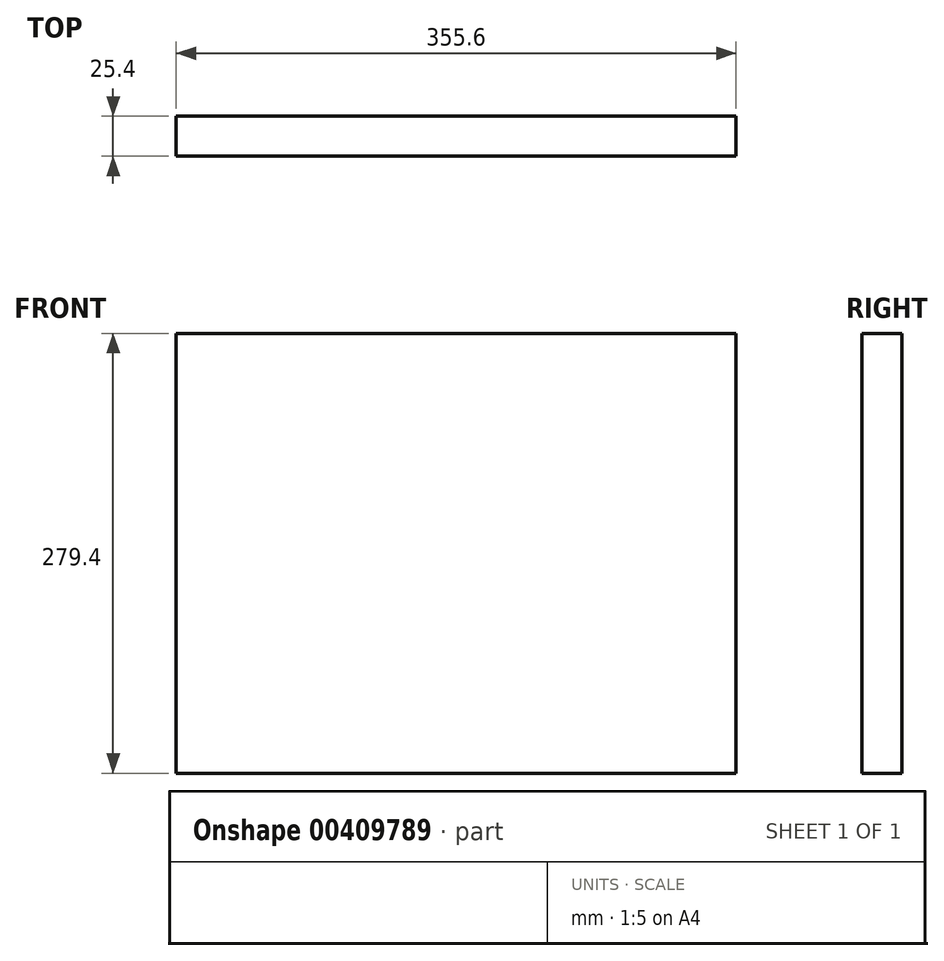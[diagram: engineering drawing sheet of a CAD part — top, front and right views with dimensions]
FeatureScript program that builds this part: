
annotation { "Feature Type Name" : "Feature", "Feature Type Description" : "" }
export const myFeature = defineFeature(function(context is Context, id is Id, definition is map)
    precondition{}
    {
        {
            var Q0;
            Q0=qCreatedBy(makeId("Front.planeOp"),FACE);
            var sketch = newSketch(context, id + "F0", { "sketchPlane" : qUnion([Q0])});
            skLineSegment(sketch, "E0.bottom", {"start": v(177.8, -139.7) * mm, "end": v(-177.8, -139.7) * mm});
            skLineSegment(sketch, "E0.top", {"start": v(177.8, 139.7) * mm, "end": v(-177.8, 139.7) * mm});
            skLineSegment(sketch, "E0.left", {"start": v(177.8, -139.7) * mm, "end": v(177.8, 139.7) * mm});
            skLineSegment(sketch, "E0.right", {"start": v(-177.8, -139.7) * mm, "end": v(-177.8, 139.7) * mm});
            skPoint(sketch, "E0.middle", {"position": v(0, 0) * mm});
            skSolve(sketch);
        }
        {
            var Q0;
            Q0=makeQuery(id+"F0.imprint","IMPRINT",FACE,{"disambiguationData":[TD([[makeQuery(id+"F0.imprint","IMPRINT",EDGE,{"derivedFrom":sQuery(id+"F0.wireOp",EDGE,"E0.bottom")}),-1.0]])]});
            extrude(context, id + "F1", {"entities" : qUnion([Q0]), "depth" : 25.4 * mm});
        }
    });
